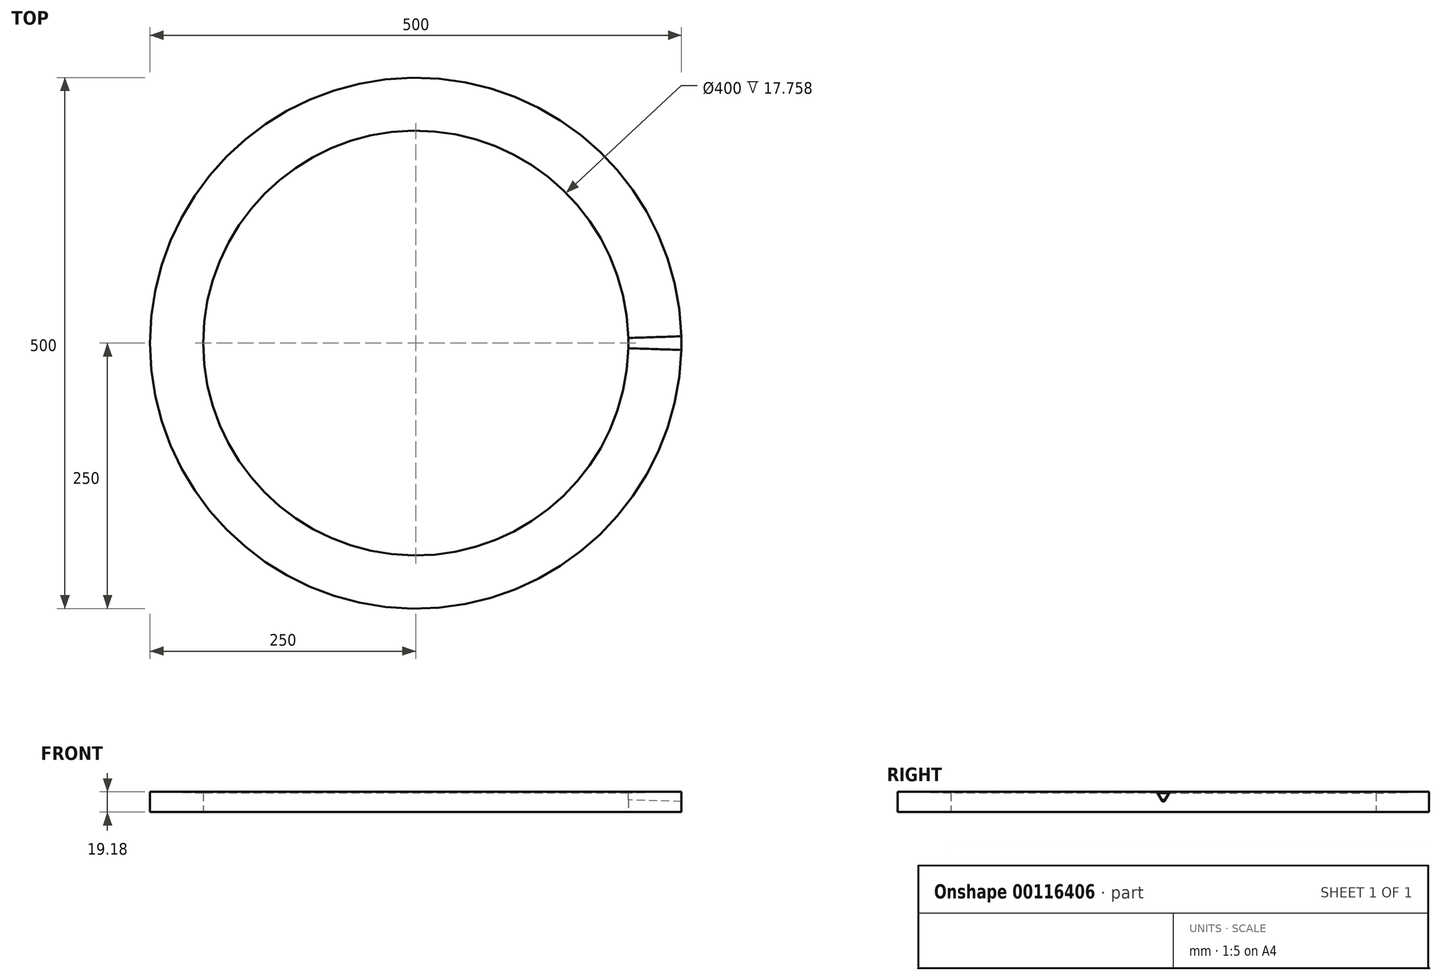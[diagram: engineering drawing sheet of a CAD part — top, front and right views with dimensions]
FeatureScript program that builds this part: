
annotation { "Feature Type Name" : "Feature", "Feature Type Description" : "" }
export const myFeature = defineFeature(function(context is Context, id is Id, definition is map)
    precondition{}
    {
        {
            assignVariable(context, id + "F0", {"name" : "r", "anyValue" : 200});
        }
        {
            assignVariable(context, id + "F1", {"name" : "R", "anyValue" : 250});
        }
        {
            var Q0;
            Q0=qCreatedBy(makeId("Right.planeOp"),FACE);
            cPlane(context, id + "F2", {"entities" : qUnion([Q0]), "cplaneType" : CPlaneType.OFFSET, "offset" : (getVariable(context, 'r')) * mm, "width" : 150 * mm, "height" : 150 * mm});
        }
        {
            var Q0;
            Q0=qCreatedBy(makeId("Right.planeOp"),FACE);
            cPlane(context, id + "F3", {"entities" : qUnion([Q0]), "cplaneType" : CPlaneType.OFFSET, "offset" : (getVariable(context, 'R')) * mm, "width" : 150 * mm, "height" : 150 * mm});
        }
        {
            var Q0;
            Q0=qCreatedBy(id+"F2.planeOp",FACE);
            var Q1;
            Q1=qCreatedBy(id+"F3.planeOp",FACE);
            cPlane(context, id + "F4", {"entities" : qUnion([Q0, Q1]), "cplaneType" : CPlaneType.MID_PLANE, "offset" : 25 * mm, "width" : 150 * mm, "height" : 150 * mm});
        }
        {
            var Q0;
            Q0=qCreatedBy(makeId("Top.planeOp"),FACE);
            var sketch = newSketch(context, id + "F5", { "sketchPlane" : qUnion([Q0])});
            skLineSegment(sketch, "E0", {"start": v(0, 0) * mm, "end": v(225, 0) * mm, "construction": true});
            skLineSegment(sketch, "E1", {"start": v(0, 0) * mm, "end": v(225, 7.37) * mm, "construction": true});
            skSolve(sketch);
        }
        {
            var Q0;
            Q0=qCreatedBy(id+"F4.planeOp",FACE);
            var sketch = newSketch(context, id + "F6", { "sketchPlane" : qUnion([Q0])});
            skLineSegment(sketch, "E2", {"start": v(0, 0) * mm, "end": v(7.37, 0) * mm, "construction": true});
            skLineSegment(sketch, "E3", {"start": v(7.37, 0) * mm, "end": v(7.37, 12.76) * mm, "construction": true});
            skLineSegment(sketch, "E4", {"start": v(7.37, 12.76) * mm, "end": v(0, 0) * mm, "construction": true});
            skCircle(sketch, "E5", {"center": v(0, 4) * mm, "radius": 2 * mm, "construction": true});
            skCircle(sketch, "E6", {"center": v(7.37, 8.76) * mm, "radius": 2 * mm, "construction": true});
            skPoint(sketch, "E7", {"position": v(5.63, 9.76) * mm});
            skSolve(sketch);
        }
        {
            var Q0;
            Q0=qCreatedBy(makeId("Front.planeOp"),FACE);
            var sketch = newSketch(context, id + "F7", { "sketchPlane" : qUnion([Q0])});
            skLineSegment(sketch, "E8", {"start": v(225, 2) * mm, "end": v(225, 9.76) * mm, "construction": true});
            skLineSegment(sketch, "E9", {"start": v(200, 9.05) * mm, "end": v(250, 10.47) * mm});
            skLineSegment(sketch, "E10", {"start": v(200, 2.7) * mm, "end": v(250, 1.3) * mm, "construction": true});
            skLineSegment(sketch, "E11", {"start": v(250, 1.3) * mm, "end": v(250, 10.47) * mm});
            skLineSegment(sketch, "E12", {"start": v(200, 9.05) * mm, "end": v(200, 2.7) * mm});
            skLineSegment(sketch, "E13", {"start": v(225, 2) * mm, "end": v(225, 0) * mm, "construction": true});
            skLineSegment(sketch, "E14", {"start": v(225, 0) * mm, "end": v(232.37, 12.76) * mm, "construction": true});
            skLineSegment(sketch, "E15", {"start": v(232.37, 12.76) * mm, "end": v(232.37, 0) * mm, "construction": true});
            skLineSegment(sketch, "E16", {"start": v(232.37, 0) * mm, "end": v(225, 0) * mm, "construction": true});
            skCircle(sketch, "E17", {"center": v(225, 4) * mm, "radius": 2 * mm, "construction": true});
            skCircle(sketch, "E18", {"center": v(232.37, 8.76) * mm, "radius": 2 * mm, "construction": true});
            skPoint(sketch, "E19", {"position": v(225, 2) * mm});
            skPoint(sketch, "E20", {"position": v(230.63, 9.76) * mm});
            skLineSegment(sketch, "E21", {"start": v(225, 9.76) * mm, "end": v(230.63, 9.76) * mm, "construction": true});
            skLineSegment(sketch, "E22", {"start": v(250, 1.3) * mm, "end": v(250, -8.7) * mm});
            skLineSegment(sketch, "E23", {"start": v(250, -8.7) * mm, "end": v(200, -8.7) * mm});
            skLineSegment(sketch, "E24", {"start": v(200, -8.7) * mm, "end": v(200, 2.7) * mm});
            skLineSegment(sketch, "E25", {"start": v(0, 0) * mm, "end": v(0, 12.76) * mm});
            skSolve(sketch);
        }
        {
            var Q0;
            Q0=qCreatedBy(id+"F3.planeOp",FACE);
            var sketch = newSketch(context, id + "F8", { "sketchPlane" : qUnion([Q0])});
            skLineSegment(sketch, "E26", {"start": v(6.45, 10.47) * mm, "end": v(1.73, 2.3) * mm});
            skLineSegment(sketch, "E27", {"start": v(6.45, 10.47) * mm, "end": v(-6.45, 10.47) * mm});
            skLineSegment(sketch, "E28", {"start": v(-6.45, 10.47) * mm, "end": v(-1.73, 2.3) * mm});
            skArc(sketch, "E29", {"start": v(-1.73, 2.3) * mm, "mid": v(0, 1.3) * mm, "end": v(1.73, 2.3) * mm});
            skSolve(sketch);
        }
        {
            var Q0;
            Q0=qCreatedBy(makeId("Front.planeOp"),FACE);
            var sketch = newSketch(context, id + "F9", { "sketchPlane" : qUnion([Q0])});
            skLineSegment(sketch, "E30", {"start": v(250, 1.3) * mm, "end": v(195, 2.85) * mm});
            skSolve(sketch);
        }
        {
            var Q0;
            Q0 = qSketchRegion(id + "F7", true);
            var Q1;
            Q1=sQuery(id+"F7.wireOp",EDGE,"E25");
            revolve(context, id + "F10", {"entities" : qUnion([Q0]), "axis" : qUnion([Q1]), "revolveType" : RevolveType.FULL});
        }
        {
            var Q0;
            Q0 = qSketchRegion(id + "F8", true);
            var Q1;
            Q1=sQuery(id+"F9.wireOp",EDGE,"E30");
            sweep(context, id + "F11", {"operationType" : NewBodyOperationType.REMOVE, "profiles" : qUnion([Q0]), "path" : qUnion([Q1])});
        }
    });
